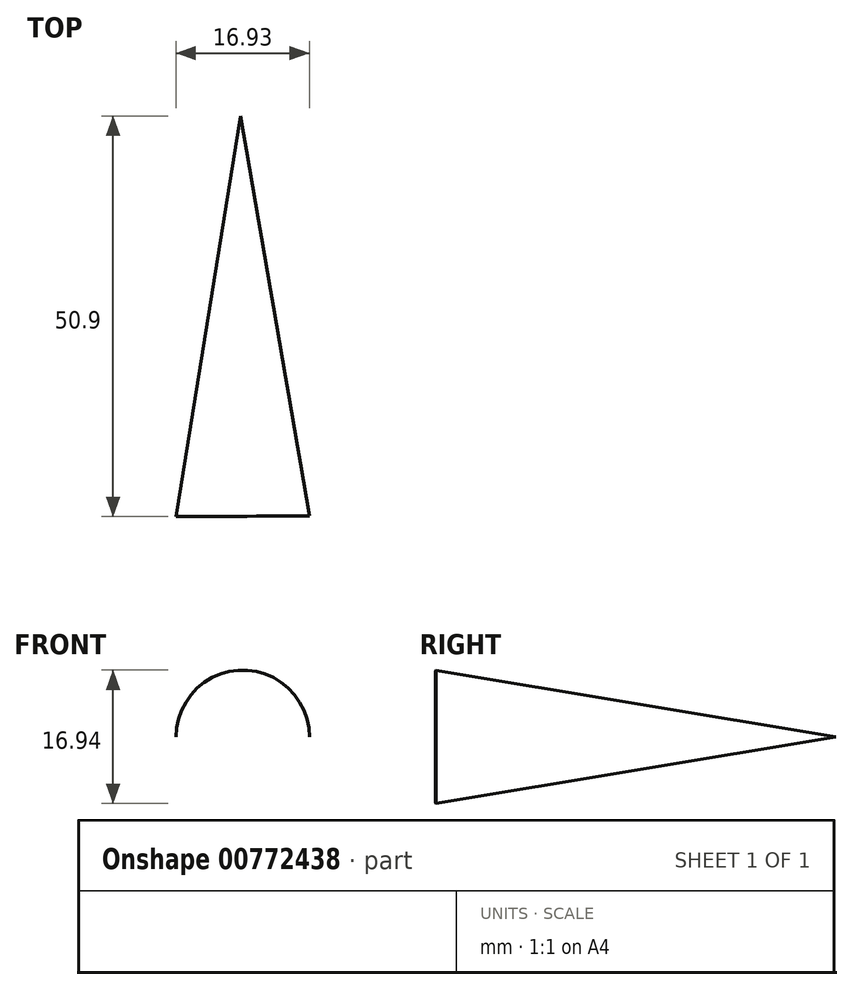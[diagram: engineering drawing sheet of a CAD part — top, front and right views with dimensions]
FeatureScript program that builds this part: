
annotation { "Feature Type Name" : "Feature", "Feature Type Description" : "" }
export const myFeature = defineFeature(function(context is Context, id is Id, definition is map)
    precondition{}
    {
        {
            var Q0;
            Q0=qCreatedBy(makeId("Top.planeOp"),FACE);
            var sketch = newSketch(context, id + "F0", { "sketchPlane" : qUnion([Q0])});
            skLineSegment(sketch, "E0", {"start": v(101.85, 0) * mm, "end": v(110.32, 0) * mm});
            skLineSegment(sketch, "E1", {"start": v(110.32, 0) * mm, "end": v(101.56, 50.8) * mm});
            skLineSegment(sketch, "E2", {"start": v(101.56, 50.8) * mm, "end": v(101.85, 0) * mm});
            skSolve(sketch);
        }
        {
            var Q0;
            Q0=makeQuery(id+"F0.imprint","IMPRINT",FACE,{"disambiguationData":[TD([[makeQuery(id+"F0.imprint","IMPRINT",EDGE,{"derivedFrom":sQuery(id+"F0.wireOp",EDGE,"E0")}),1.0]])]});
            var Q1;
            Q1=sQuery(id+"F0.wireOp",EDGE,"E2");
            revolve(context, id + "F1", {"surfaceOperationType" : NewSurfaceOperationType.NEW, "entities" : qUnion([Q0]), "axis" : qUnion([Q1]), "revolveType" : RevolveType.FULL});
        }
    });
